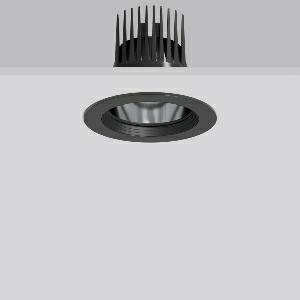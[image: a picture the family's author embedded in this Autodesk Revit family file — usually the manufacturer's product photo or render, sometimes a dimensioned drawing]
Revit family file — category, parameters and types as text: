
# Revit family: heledon_maxi_e_901757_003_2_76_7148
name_source: partatom
category: Lighting Fixtures
units: mm (PartAtom-declared; Revit-internal decimal feet)

## family parameters
Cut with Voids When Loaded = No
Host = Face
Light Source = No
Part Type = Normal
Room Calculation Point = No
Round Connector Dimension = Use Diameter
Shared = No

## types (1)
- HELEDON maxi E (1 x LED Modul 927, 3150 lm, 2700)
    Apparent Load = 25 VA
    Approval mark = CE
    CIE Flux Codes = 100 100 100 100 100
    Color Rendering = 92
    Color Temperature = 2700
    Default Elevation = 1800 mm
    Description = Series: HELEDON maxi
Round recessed downlight. Housing: die-cast aluminium, powder-coated. Black plastic ring and recessed LED to prevent glare from the side. Optical assembly with reflector made of MIRO-Silver with 98% total light reflection for outstanding efficiency - can be changed without tools. Best colour rendering index Ra>90. Suitable for Recessed ceiling mounting. Installation without tools thanks to spring fastening system. Including separate LED converter with connecting cable 600 mm.High quality converter without flickering and stroboscopic effect. Through-wiring box (5 pole) available as accessory. The following accessories can be mounted without use of tools: interchangeable lenses, decorative glasses, honeycomb louvre, clear and frosted diffusers, white interchangeable plastic ring. 
Colour: deep black, matt (RAL 9005)
Diameter: 162 mm
Height: 3 mm
Cut-out diameter: 152 mm
Recess height: 200 mm
Luminaire: recess height: 135 mm
Lamp: LED
Socket: without socket
Colour temperature: 2700K
Colour rendering index (CRI): 92
System power: 25 W
Rated luminous flux: 3150 lm
Luminous efficiency: 126 lm/W
Control gear: Converter, dimmable, DALI
Protection class: II
Type of protection: IP 20
    Height = 0 mm  [stored 0 ft]
    Lamp = 1 x LED Modul 927
    Lamp Light Flux = 3150 lm
    Lamp count = 1
    Length = 162 mm
    Lifetime = 50000 h
    Luminous efficacy = 126 lm/W
    Manufacturer = RZB
    ModVariant = No
    Model = 901757.003.2.76
    Mounting Place = Ceiling
    Mounting Type = Recessed
    Number of Poles = 1
    OnlyDefault = Yes
    Power Factor = 1
    Product Name = HELEDON maxi E
    Product group = Recessed downlights
    ProductGroupID = 402
    Protection Class = Protection class II
    Protection Degree = IP 20
    RLX_Detail_Level = 1
    RLX_Emergency_Light_Flux = 0 lm
    RLX_Emergency_Type = 0
    RLX_Emergency_Type_DB = No
    RlxData = <blob elided: 119597 chars, md5=d96548da>
    Socket = socket
    Standby Power = 0 W
    System Light Flux = 3150 lm
    System Power = 25 W
    Type Comments = Product without accessories
    Type Image = 901662.003.jpg
    URL = http://relux.com
    VarID = ---
    Voltage = 230 V
    Voltage Range = 220-240 V
    Weight = 0.00 kg
    Width = 0 mm  [stored 0 ft]

note: [stored X ft] marks values corroborated as IEEE doubles in the binary element streams (Revit-internal decimal feet)

## geometry (parser evidence)
native form markers: Blend x4, Sweep x11
no freeform markers — native parametric forms only
